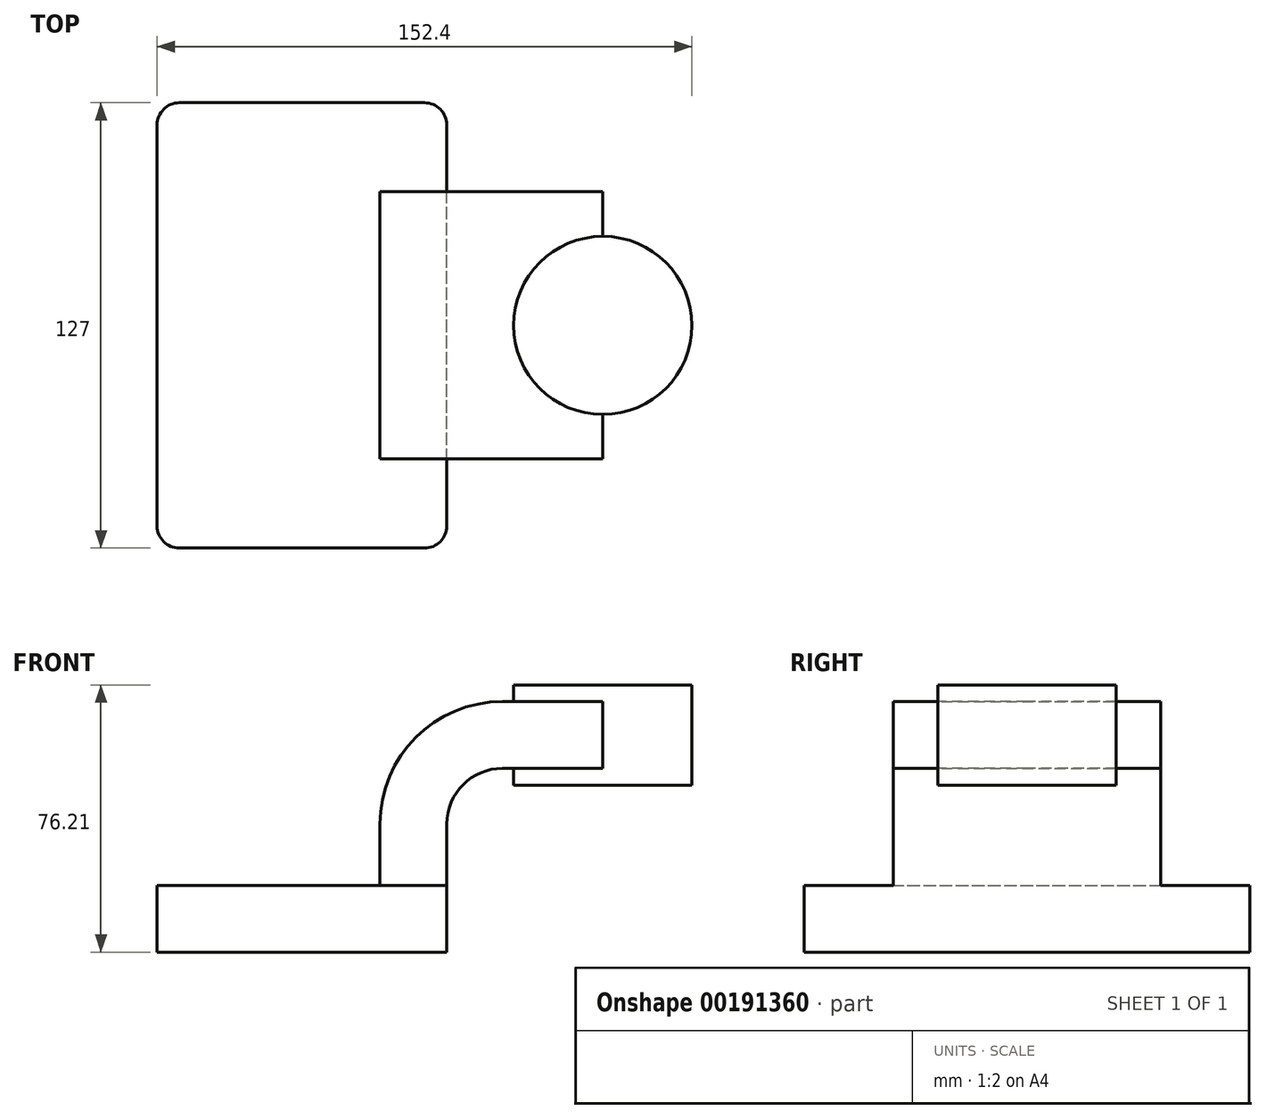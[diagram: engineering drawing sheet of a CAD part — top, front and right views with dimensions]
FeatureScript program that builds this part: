
annotation { "Feature Type Name" : "Feature", "Feature Type Description" : "" }
export const myFeature = defineFeature(function(context is Context, id is Id, definition is map)
    precondition{}
    {
        {
            var Q0;
            Q0=qCreatedBy(makeId("Front.planeOp"),FACE);
            var sketch = newSketch(context, id + "F0", { "sketchPlane" : qUnion([Q0])});
            skLineSegment(sketch, "E0.bottom", {"start": v(-41.28, -9.53) * mm, "end": v(41.28, -9.53) * mm});
            skLineSegment(sketch, "E0.top", {"start": v(-41.28, 9.53) * mm, "end": v(41.28, 9.53) * mm});
            skLineSegment(sketch, "E0.left", {"start": v(-41.28, -9.53) * mm, "end": v(-41.28, 9.53) * mm});
            skLineSegment(sketch, "E0.right", {"start": v(41.28, -9.53) * mm, "end": v(41.28, 9.52) * mm});
            skPoint(sketch, "E0.middle", {"position": v(0, 0) * mm});
            skLineSegment(sketch, "E1.bottom", {"start": v(60.32, 66.67) * mm, "end": v(111.12, 66.67) * mm});
            skLineSegment(sketch, "E1.top", {"start": v(60.33, 38.1) * mm, "end": v(111.12, 38.1) * mm});
            skLineSegment(sketch, "E1.left", {"start": v(60.32, 66.67) * mm, "end": v(60.33, 38.1) * mm});
            skLineSegment(sketch, "E1.right", {"start": v(111.12, 66.67) * mm, "end": v(111.12, 38.1) * mm});
            skPoint(sketch, "E1.middle", {"position": v(85.72, 52.39) * mm});
            skLineSegment(sketch, "E2", {"start": v(41.28, 9.53) * mm, "end": v(41.28, 27) * mm});
            skArc(sketch, "E3", {"start": v(41.28, 27) * mm, "mid": v(45.92, 38.23) * mm, "end": v(57.15, 42.88) * mm});
            skLineSegment(sketch, "E4", {"start": v(57.15, 42.88) * mm, "end": v(85.72, 42.88) * mm});
            skLineSegment(sketch, "E5.0", {"start": v(57.15, 61.93) * mm, "end": v(85.72, 61.93) * mm});
            skArc(sketch, "E5.1", {"start": v(22.23, 27) * mm, "mid": v(32.45, 51.7) * mm, "end": v(57.15, 61.93) * mm});
            skLineSegment(sketch, "E5.2", {"start": v(22.23, 9.53) * mm, "end": v(22.23, 27) * mm});
            skLineSegment(sketch, "E6", {"start": v(85.72, 38.1) * mm, "end": v(85.72, 66.67) * mm});
            skFitSpline(sketch, "E7", {"points": [v(-41.28, 9.53) * mm, v(57.15, 61.93) * mm], "startDerivative": vector(3.01, 84.5) * mm, "endDerivative": vector(171.45, -1.33) * mm});
            skSolve(sketch);
        }
        {
            var Q0;
            Q0=makeQuery(id+"F0.imprint","IMPRINT",FACE,{"disambiguationData":[TD([[makeQuery(id+"F0.imprint","IMPRINT",EDGE,{"derivedFrom":sQuery(id+"F0.wireOp",EDGE,"E0.bottom")}),1.0]])]});
            extrude(context, id + "F1", {"entities" : qUnion([Q0]), "endBound" : BoundingType.SYMMETRIC, "depth" : 127 * mm});
        }
        {
            var Q0;
            {var subQ0=sQuery(id+"F0.wireOp",EDGE,"E5.0");var subQ1=sQuery(id+"F0.wireOp",EDGE,"E1.left");var subQ2=makeQuery(id+"F0.imprint","INTERSECT",VERTEX,{"derivedFrom":[subQ1,subQ0]});Q0=makeQuery(id+"F0.imprint","IMPRINT",FACE,{"disambiguationData":[TD([[makeQuery(id+"F0.imprint","IMPRINT",EDGE,{"disambiguationData":[TD([[subQ2,-1.0]])],"derivedFrom":subQ1}),1.0]])]});}
            var Q1;
            {var subQ1=sQuery(id+"F0.wireOp",EDGE,"E2");Q1=makeQuery(id+"F0.imprint","IMPRINT",FACE,{"disambiguationData":[TD([[makeQuery(id+"F0.imprint","IMPRINT",EDGE,{"derivedFrom":subQ1}),1.0]])]});}
            extrude(context, id + "F2", {"entities" : qUnion([Q0, Q1]), "operationType" : NewBodyOperationType.ADD, "endBound" : BoundingType.SYMMETRIC, "depth" : 76.2 * mm});
        }
        {
            var Q0;
            Q0=makeQuery(id+"F0.imprint","IMPRINT",FACE,{"disambiguationData":[TD([[makeQuery(id+"F0.imprint","IMPRINT",EDGE,{"derivedFrom":sQuery(id+"F0.wireOp",EDGE,"E5.1")}),1.0]])]});
            extrude(context, id + "F3", {"entities" : qUnion([Q0]), "operationType" : NewBodyOperationType.ADD, "endBound" : BoundingType.SYMMETRIC, "depth" : 19.05 * mm});
        }
        {
            var Q0;
            {var subQ0=sQuery(id+"F0.wireOp",EDGE,"E1.right");Q0=makeQuery(id+"F0.imprint","IMPRINT",FACE,{"disambiguationData":[TD([[makeQuery(id+"F0.imprint","IMPRINT",EDGE,{"derivedFrom":subQ0}),-1.0]])]});}
            var Q1;
            Q1=sQuery(id+"F0.wireOp",EDGE,"E6");
            revolve(context, id + "F4", {"operationType" : NewBodyOperationType.ADD, "entities" : qUnion([Q0]), "axis" : qUnion([Q1]), "revolveType" : RevolveType.FULL});
        }
        {
            var Q0;
            Q0=makeQuery(id+"F1.opExtrude","CAP_EDGE",EDGE,{"disambiguationData":[OSD([sQuery(id+"F0.wireOp",EDGE,"E0.left")])],"isStart":false});
            var Q1;
            Q1=makeQuery(id+"F1.opExtrude","CAP_EDGE",EDGE,{"disambiguationData":[OSD([sQuery(id+"F0.wireOp",EDGE,"E0.right")])],"isStart":false});
            var Q2;
            Q2=makeQuery(id+"F1.opExtrude","CAP_EDGE",EDGE,{"disambiguationData":[OSD([sQuery(id+"F0.wireOp",EDGE,"E0.left")])],"isStart":true});
            var Q3;
            Q3=makeQuery(id+"F1.opExtrude","CAP_EDGE",EDGE,{"disambiguationData":[OSD([sQuery(id+"F0.wireOp",EDGE,"E0.right")])],"isStart":true});
            fillet(context, id + "F5", {"entities" : qUnion([Q0, Q1, Q2, Q3]), "radius" : 6.35 * mm, "tangentPropagation" : true, "allowEdgeOverflow" : false});
        }
    });
